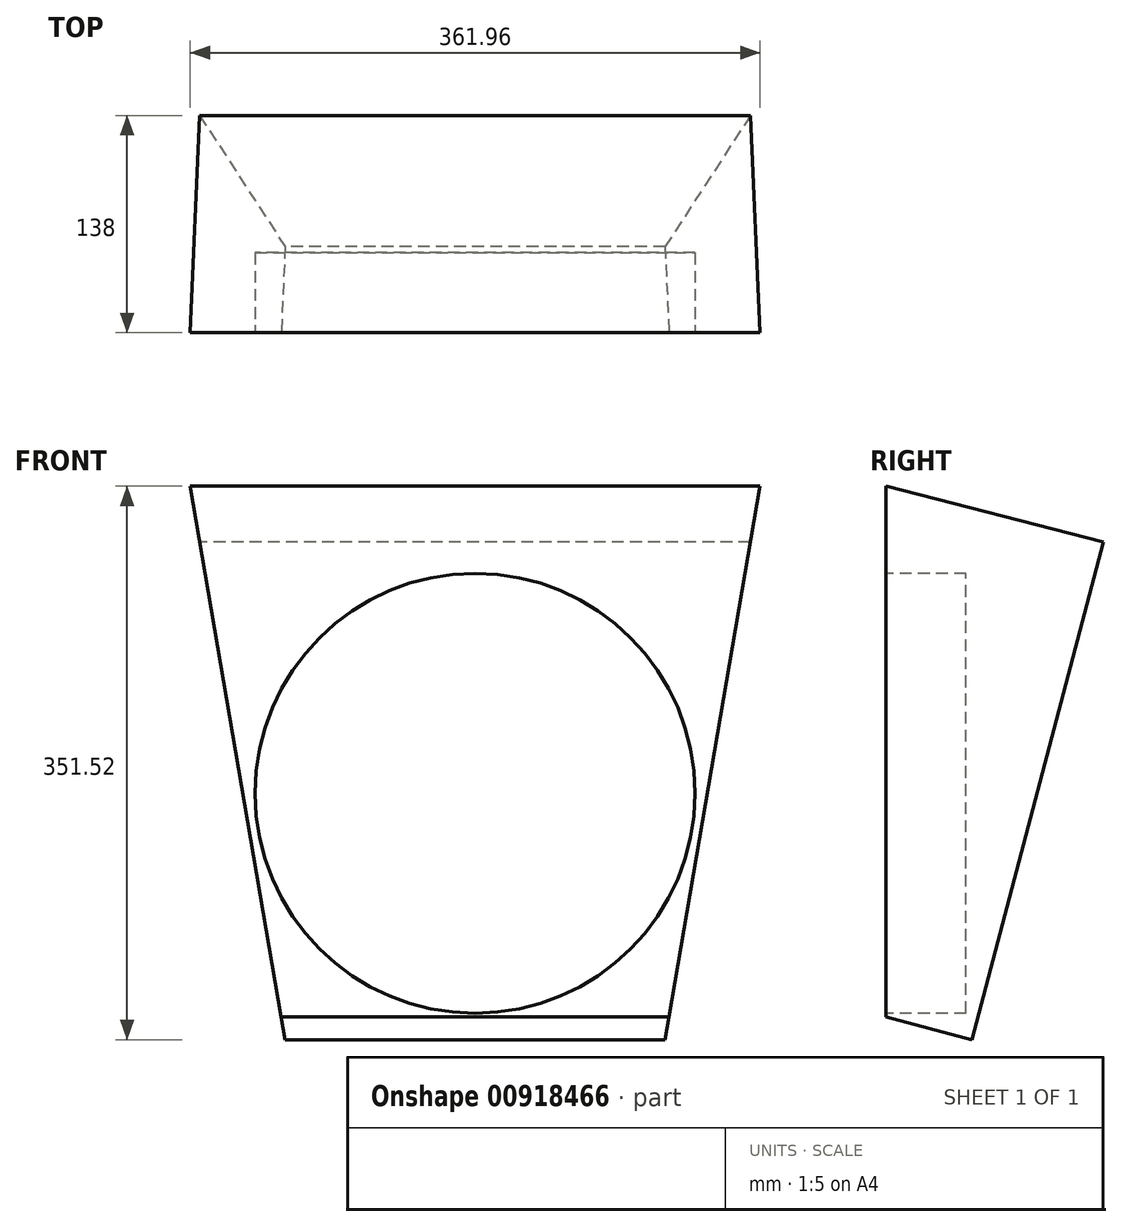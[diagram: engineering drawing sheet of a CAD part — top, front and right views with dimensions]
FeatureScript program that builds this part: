
annotation { "Feature Type Name" : "Feature", "Feature Type Description" : "" }
export const myFeature = defineFeature(function(context is Context, id is Id, definition is map)
    precondition{}
    {
        {
            var Q0;
            Q0=qCreatedBy(makeId("Right.planeOp"),FACE);
            var sketch = newSketch(context, id + "F0", { "sketchPlane" : qUnion([Q0])});
            skLineSegment(sketch, "E0.0", {"start": v(-41.3, 234.68) * mm, "end": v(96.7, 199.12) * mm});
            skLineSegment(sketch, "E0.1", {"start": v(-41.3, 234.68) * mm, "end": v(-41.3, -100.43) * mm});
            skLineSegment(sketch, "E0.2", {"start": v(96.7, 199.12) * mm, "end": v(14.07, -114.2) * mm});
            skLineSegment(sketch, "E0.3", {"start": v(13.37, -116.83) * mm, "end": v(-41.79, -102.28) * mm});
            skLineSegment(sketch, "E1", {"start": v(-41.3, -100.43) * mm, "end": v(-41.3, -102.41) * mm});
            skLineSegment(sketch, "E2", {"start": v(14.07, -114.2) * mm, "end": v(13.37, -116.83) * mm});
            skSolve(sketch);
        }
        {
            var Q0;
            Q0=qSketchRegion(id+"F0",true);
            extrude(context, id + "F1", {"entities" : qUnion([Q0]), "endBound" : BoundingType.SYMMETRIC, "depth" : 361.95 * mm, "offsetDistance" : 25.4 * mm});
        }
        {
            var Q0;
            Q0=makeQuery(id+"F1.opExtrude","SWEPT_BODY",BODY,{"disambiguationData":[OSD([sQuery(id+"F0.wireOp",EDGE,"E0.0"),sQuery(id+"F0.wireOp",EDGE,"E0.1"),sQuery(id+"F0.wireOp",EDGE,"E0.2"),sQuery(id+"F0.wireOp",EDGE,"E0.3"),sQuery(id+"F0.wireOp",EDGE,"E1"),sQuery(id+"F0.wireOp",EDGE,"E2")])]});
            transform(context, id + "F2", {"entities" : qUnion([Q0]), "transformType" : TransformType.TRANSLATION_3D, "dx" : 0 * mm, "dy" : 41.3 * mm, "dz" : -26.54 * mm, "makeCopy" : false});
        }
        {
            var Q0;
            Q0=makeQuery(id+"F1.opExtrude","SWEPT_FACE",FACE,{"disambiguationData":[OSD([sQuery(id+"F0.wireOp",EDGE,"E0.1"),sQuery(id+"F0.wireOp",EDGE,"E1")])]});
            var sketch = newSketch(context, id + "F3", { "sketchPlane" : qUnion([Q0])});
            skPoint(sketch, "E3.1", {"position": v(180.98, 208.15) * mm});
            skLineSegment(sketch, "E4.1", {"start": v(120.65, -143.37) * mm, "end": v(124.62, -107.34) * mm});
            skLineSegment(sketch, "E5", {"start": v(120.65, -143.37) * mm, "end": v(180.98, 208.15) * mm});
            skLineSegment(sketch, "E6", {"start": v(120.65, -143.37) * mm, "end": v(410.7, -143.37) * mm});
            skLineSegment(sketch, "E7", {"start": v(180.98, 208.15) * mm, "end": v(410.7, -143.37) * mm});
            skLineSegment(sketch, "E8", {"start": v(0, 352.04) * mm, "end": v(0, -210.61) * mm, "construction": true});
            skLineSegment(sketch, "E9.MirrorCS", {"start": v(-120.65, -143.37) * mm, "end": v(-124.62, -107.34) * mm});
            skLineSegment(sketch, "E10.MirrorCS", {"start": v(-120.65, -143.37) * mm, "end": v(-410.7, -143.37) * mm});
            skLineSegment(sketch, "E11.MirrorCS", {"start": v(-180.97, 208.15) * mm, "end": v(-410.7, -143.37) * mm});
            skPoint(sketch, "E12.MirrorP", {"position": v(-180.98, 208.15) * mm});
            skLineSegment(sketch, "E13.MirrorCS", {"start": v(-120.65, -143.37) * mm, "end": v(-180.98, 208.15) * mm});
            skSolve(sketch);
        }
        {
            var Q0;
            Q0=qSketchRegion(id+"F3",true);
            extrude(context, id + "F4", {"entities" : qUnion([Q0]), "operationType" : NewBodyOperationType.REMOVE, "endBound" : BoundingType.SYMMETRIC, "oppositeDirection" : true, "depth" : 304.8 * mm, "offsetDistance" : 25.4 * mm});
        }
        {
            var Q0;
            Q0=qCreatedBy(makeId("Front.planeOp"),FACE);
            var sketch = newSketch(context, id + "F5", { "sketchPlane" : qUnion([Q0])});
            skCircle(sketch, "E14", {"center": v(0, 13.13) * mm, "radius": 139.7 * mm});
            skSolve(sketch);
        }
        {
            var Q0;
            Q0=qSketchRegion(id+"F5",true);
            extrude(context, id + "F6", {"entities" : qUnion([Q0]), "oppositeDirection" : true, "depth" : 50.8 * mm, "offsetDistance" : 25.4 * mm});
        }
    });
